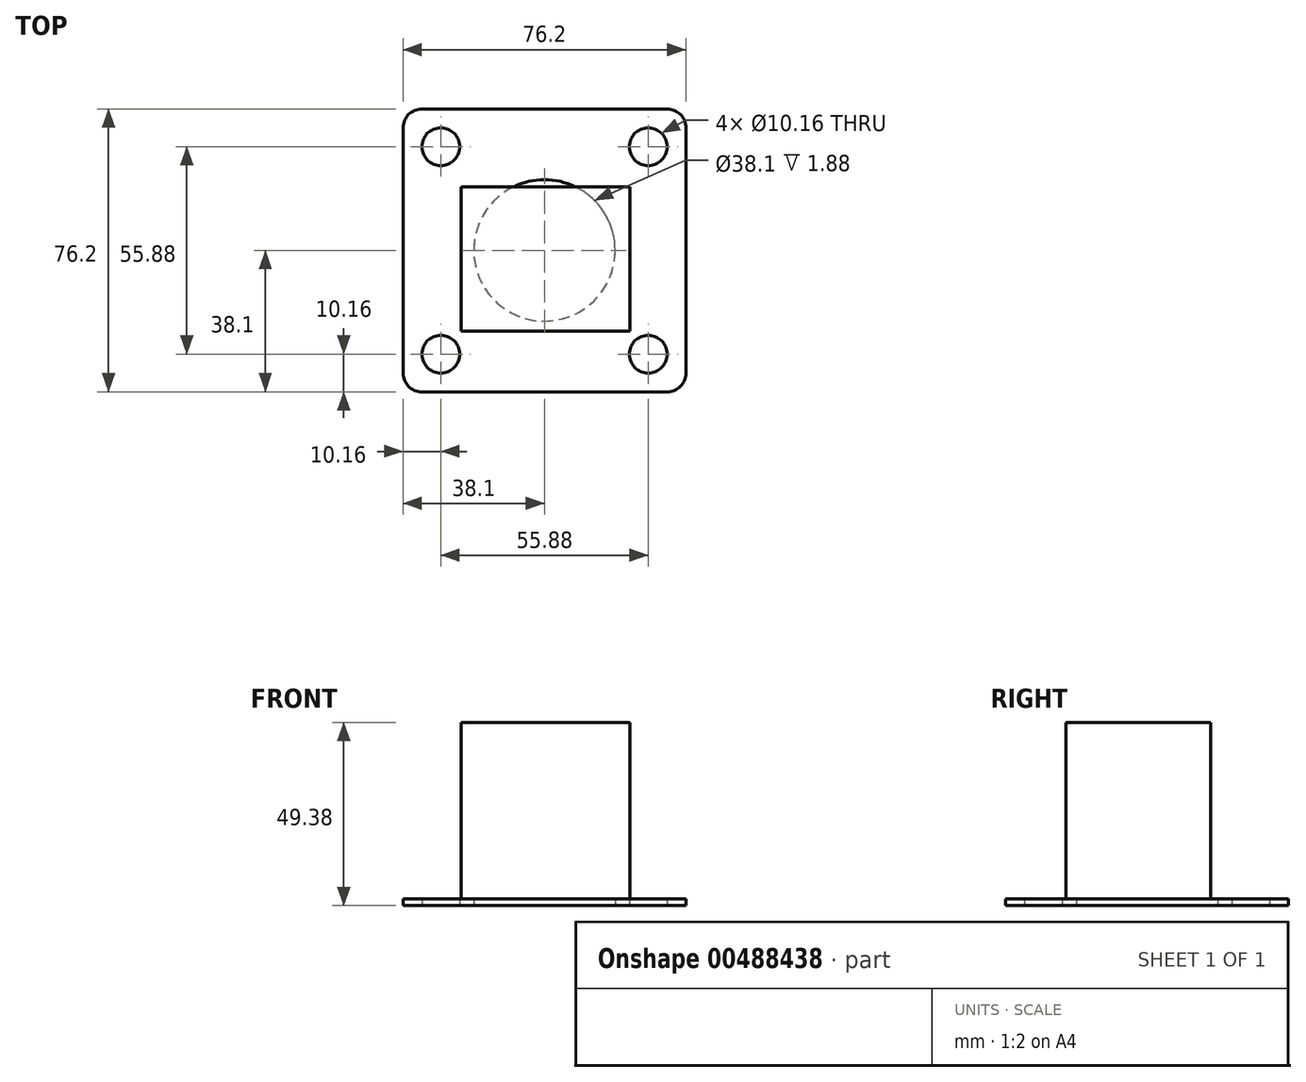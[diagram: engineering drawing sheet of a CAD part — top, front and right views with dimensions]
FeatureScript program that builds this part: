
annotation { "Feature Type Name" : "Feature", "Feature Type Description" : "" }
export const myFeature = defineFeature(function(context is Context, id is Id, definition is map)
    precondition{}
    {
        {
            var Q0;
            Q0=qCreatedBy(makeId("Top.planeOp"),FACE);
            var sketch = newSketch(context, id + "F0", { "sketchPlane" : qUnion([Q0])});
            skLineSegment(sketch, "E0.bottom", {"start": v(38.1, 38.1) * mm, "end": v(-38.1, 38.1) * mm});
            skLineSegment(sketch, "E0.top", {"start": v(38.1, -38.1) * mm, "end": v(-38.1, -38.1) * mm});
            skLineSegment(sketch, "E0.left", {"start": v(38.1, 38.1) * mm, "end": v(38.1, -38.1) * mm});
            skLineSegment(sketch, "E0.right", {"start": v(-38.1, 38.1) * mm, "end": v(-38.1, -38.1) * mm});
            skPoint(sketch, "E0.middle", {"position": v(0, 0) * mm});
            skCircle(sketch, "E1", {"center": v(0, 0) * mm, "radius": 19.05 * mm});
            skLineSegment(sketch, "E2.bottom", {"start": v(27.94, 27.94) * mm, "end": v(-27.94, 27.94) * mm, "construction": true});
            skLineSegment(sketch, "E2.top", {"start": v(27.94, -27.94) * mm, "end": v(-27.94, -27.94) * mm, "construction": true});
            skLineSegment(sketch, "E2.left", {"start": v(27.94, 27.94) * mm, "end": v(27.94, -27.94) * mm, "construction": true});
            skLineSegment(sketch, "E2.right", {"start": v(-27.94, 27.94) * mm, "end": v(-27.94, -27.94) * mm, "construction": true});
            skCircle(sketch, "E3", {"center": v(-27.94, 27.94) * mm, "radius": 5.08 * mm});
            skCircle(sketch, "E4", {"center": v(27.94, 27.94) * mm, "radius": 5.08 * mm});
            skCircle(sketch, "E5", {"center": v(-27.94, -27.94) * mm, "radius": 5.08 * mm});
            skCircle(sketch, "E6", {"center": v(27.94, -27.94) * mm, "radius": 5.08 * mm});
            skSolve(sketch);
        }
        {
            var Q0;
            Q0 = qSketchRegion(id + "F0", true);
            extrude(context, id + "F1", {"entities" : qUnion([Q0]), "depth" : 1.88 * mm});
        }
        {
            var Q0;
            Q0=makeQuery(id+"F1.opExtrude","SWEPT_EDGE",EDGE,{"disambiguationData":[OSD([sQuery(id+"F0.wireOp",EDGE,"E0.top"),sQuery(id+"F0.wireOp",EDGE,"E0.right")])]});
            var Q1;
            Q1=makeQuery(id+"F1.opExtrude","SWEPT_EDGE",EDGE,{"disambiguationData":[OSD([sQuery(id+"F0.wireOp",EDGE,"E0.top"),sQuery(id+"F0.wireOp",EDGE,"E0.left")])]});
            var Q2;
            Q2=makeQuery(id+"F1.opExtrude","SWEPT_EDGE",EDGE,{"disambiguationData":[OSD([sQuery(id+"F0.wireOp",EDGE,"E0.bottom"),sQuery(id+"F0.wireOp",EDGE,"E0.left")])]});
            var Q3;
            Q3=makeQuery(id+"F1.opExtrude","SWEPT_EDGE",EDGE,{"disambiguationData":[OSD([sQuery(id+"F0.wireOp",EDGE,"E0.bottom"),sQuery(id+"F0.wireOp",EDGE,"E0.right")])]});
            fillet(context, id + "F2", {"entities" : qUnion([Q0, Q1, Q2, Q3]), "radius" : 5.08 * mm, "tangentPropagation" : true, "allowEdgeOverflow" : false});
        }
        {
            var Q0;
            Q0=makeQuery(id+"F1.opExtrude","CAP_FACE",FACE,{"disambiguationData":[OSD([sQuery(id+"F0.wireOp",EDGE,"E0.bottom"),sQuery(id+"F0.wireOp",EDGE,"E0.top"),sQuery(id+"F0.wireOp",EDGE,"E0.left"),sQuery(id+"F0.wireOp",EDGE,"E0.right"),sQuery(id+"F0.wireOp",EDGE,"E1"),sQuery(id+"F0.wireOp",EDGE,"E3"),sQuery(id+"F0.wireOp",EDGE,"E4"),sQuery(id+"F0.wireOp",EDGE,"E5"),sQuery(id+"F0.wireOp",EDGE,"E6")])],"isStart":true});
            var sketch = newSketch(context, id + "F3", { "sketchPlane" : qUnion([Q0])});
            skLineSegment(sketch, "E7.0", {"start": v(33.02, 38.1) * mm, "end": v(-33.02, 38.1) * mm});
            skArc(sketch, "E7.1", {"start": v(-33.02, 38.1) * mm, "mid": v(-36.61, 36.61) * mm, "end": v(-38.1, 33.02) * mm});
            skLineSegment(sketch, "E7.2", {"start": v(-38.1, -33.02) * mm, "end": v(-38.1, 33.02) * mm});
            skArc(sketch, "E7.3", {"start": v(-38.1, -33.02) * mm, "mid": v(-36.61, -36.61) * mm, "end": v(-33.02, -38.1) * mm});
            skLineSegment(sketch, "E7.4", {"start": v(33.02, -38.1) * mm, "end": v(-33.02, -38.1) * mm});
            skArc(sketch, "E7.5", {"start": v(33.02, -38.1) * mm, "mid": v(36.61, -36.61) * mm, "end": v(38.1, -33.02) * mm});
            skLineSegment(sketch, "E7.6", {"start": v(38.1, -33.02) * mm, "end": v(38.1, 33.02) * mm});
            skArc(sketch, "E7.7", {"start": v(38.1, 33.02) * mm, "mid": v(36.61, 36.61) * mm, "end": v(33.02, 38.1) * mm});
            skSolve(sketch);
        }
        {
            var Q0;
            Q0=makeQuery(id+"F3.imprint","IMPRINT",FACE,{"disambiguationData":[TD([[makeQuery(id+"F3.imprint","IMPRINT",EDGE,{"derivedFrom":sQuery(id+"F3.wireOp",EDGE,"E7.0")}),1.0]])]});
            cPlane(context, id + "F4", {"entities" : qUnion([Q0]), "cplaneType" : CPlaneType.OFFSET, "offset" : 177.04 * mm, "width" : 152.4 * mm, "height" : 152.4 * mm});
        }
        {
            var Q0;
            Q0=makeQuery(id+"F1.opExtrude","CAP_FACE",FACE,{"disambiguationData":[OSD([sQuery(id+"F0.wireOp",EDGE,"E0.bottom"),sQuery(id+"F0.wireOp",EDGE,"E0.top"),sQuery(id+"F0.wireOp",EDGE,"E0.left"),sQuery(id+"F0.wireOp",EDGE,"E0.right"),sQuery(id+"F0.wireOp",EDGE,"E1"),sQuery(id+"F0.wireOp",EDGE,"E3"),sQuery(id+"F0.wireOp",EDGE,"E4"),sQuery(id+"F0.wireOp",EDGE,"E5"),sQuery(id+"F0.wireOp",EDGE,"E6")])],"isStart":false});
            var sketch = newSketch(context, id + "F5", { "sketchPlane" : qUnion([Q0])});
            skLineSegment(sketch, "E8.bottom", {"start": v(-22.42, 17.16) * mm, "end": v(23.05, 17.16) * mm});
            skLineSegment(sketch, "E8.top", {"start": v(-22.42, -21.8) * mm, "end": v(23.05, -21.8) * mm});
            skLineSegment(sketch, "E8.left", {"start": v(-22.42, 17.16) * mm, "end": v(-22.42, -21.8) * mm});
            skLineSegment(sketch, "E8.right", {"start": v(23.05, 17.16) * mm, "end": v(23.05, -21.8) * mm});
            skSolve(sketch);
        }
        {
            var Q0;
            Q0 = qSketchRegion(id + "F5", true);
            extrude(context, id + "F6", {"entities" : qUnion([Q0]), "operationType" : NewBodyOperationType.ADD, "depth" : 47.5 * mm, "offsetDistance" : 25.4 * mm});
        }
    });
